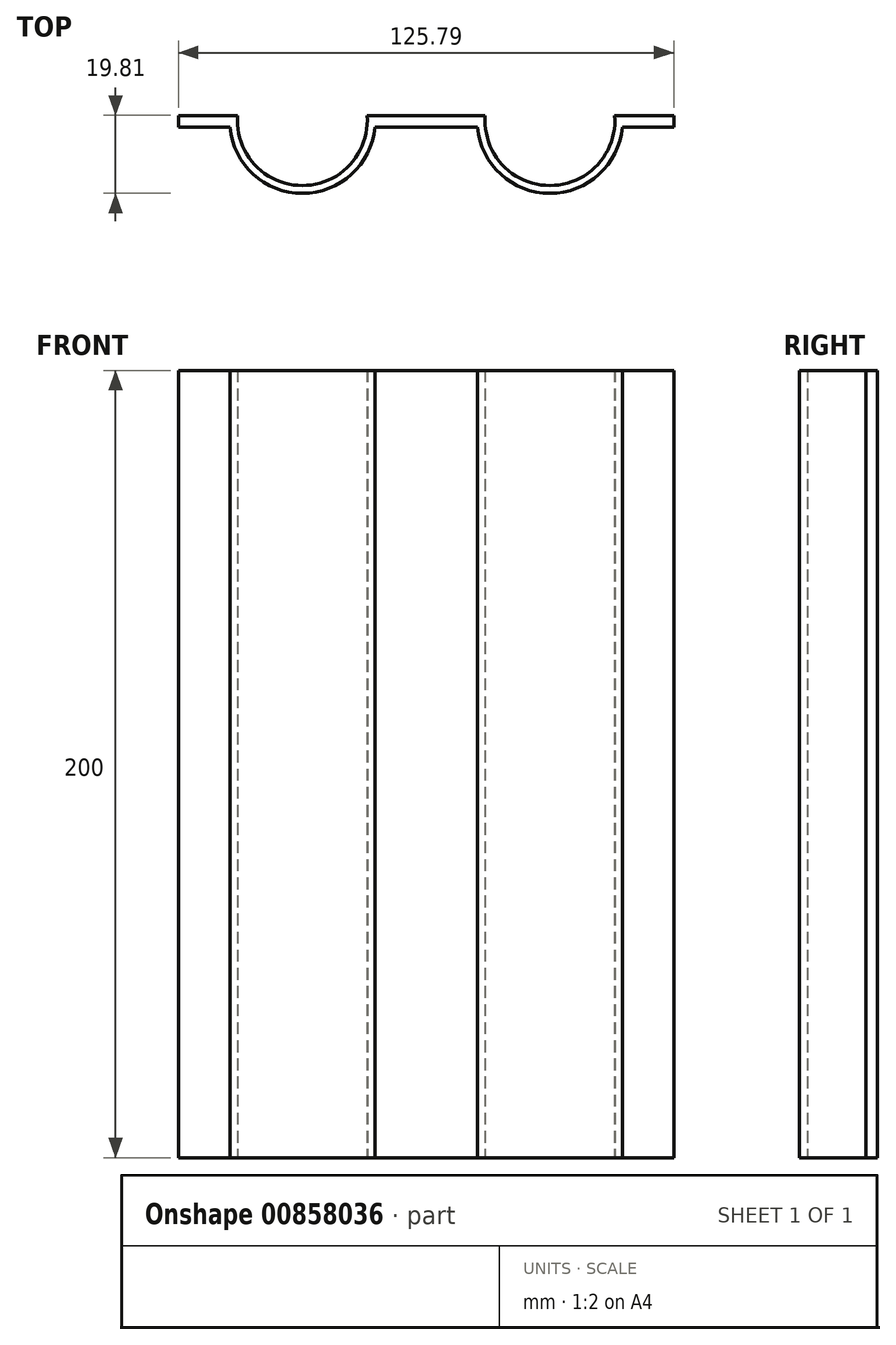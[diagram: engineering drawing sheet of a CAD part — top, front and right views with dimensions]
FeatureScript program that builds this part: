
annotation { "Feature Type Name" : "Feature", "Feature Type Description" : "" }
export const myFeature = defineFeature(function(context is Context, id is Id, definition is map)
    precondition{}
    {
        {
            var Q0;
            Q0=qCreatedBy(makeId("Top.planeOp"),FACE);
            var sketch = newSketch(context, id + "F0", { "sketchPlane" : qUnion([Q0])});
            skLineSegment(sketch, "E0", {"start": v(-51.2, 1.3) * mm, "end": v(-66.2, 1.3) * mm});
            skLineSegment(sketch, "E1", {"start": v(-66.2, 1.3) * mm, "end": v(-66.2, -1.7) * mm});
            skLineSegment(sketch, "E2", {"start": v(-66.2, -1.7) * mm, "end": v(-53.17, -1.7) * mm});
            skLineSegment(sketch, "E3", {"start": v(-18.3, 1.3) * mm, "end": v(11.7, 1.3) * mm});
            skLineSegment(sketch, "E4", {"start": v(44.6, 1.3) * mm, "end": v(59.6, 1.3) * mm});
            skLineSegment(sketch, "E5", {"start": v(59.6, 1.3) * mm, "end": v(59.6, -1.7) * mm});
            skLineSegment(sketch, "E6", {"start": v(59.6, -1.7) * mm, "end": v(46.57, -1.7) * mm});
            skLineSegment(sketch, "E7", {"start": v(9.72, -1.7) * mm, "end": v(-16.33, -1.7) * mm});
            skArc(sketch, "E8", {"start": v(-51.2, 1.3) * mm, "mid": v(-34.75, -16.5) * mm, "end": v(-18.3, 1.3) * mm});
            skArc(sketch, "E9", {"start": v(11.7, 1.3) * mm, "mid": v(28.15, -16.5) * mm, "end": v(44.6, 1.3) * mm});
            skArc(sketch, "E10.0", {"start": v(9.7, 1.47) * mm, "mid": v(9.7, 1.39) * mm, "end": v(9.7, 1.3) * mm});
            skArc(sketch, "E11.0", {"start": v(-53.2, 1.47) * mm, "mid": v(-53.2, 1.39) * mm, "end": v(-53.2, 1.3) * mm});
            skArc(sketch, "E12.trimOffspring", {"start": v(-53.17, -1.7) * mm, "mid": v(-34.75, -18.5) * mm, "end": v(-16.33, -1.7) * mm});
            skPoint(sketch, "E13.orphan", {"position": v(-51.16, -1.7) * mm});
            skArc(sketch, "E14.trimOffspring", {"start": v(-16.3, 1.3) * mm, "mid": v(-16.3, 1.39) * mm, "end": v(-16.3, 1.47) * mm});
            skArc(sketch, "E15.trimOffspring", {"start": v(9.72, -1.7) * mm, "mid": v(28.15, -18.5) * mm, "end": v(46.57, -1.7) * mm});
            skArc(sketch, "E16.trimOffspring", {"start": v(46.6, 1.3) * mm, "mid": v(46.6, 1.39) * mm, "end": v(46.59, 1.47) * mm});
            skSolve(sketch);
        }
        {
            var Q0;
            {var subQ10=sQuery(id+"F0.wireOp",EDGE,"E1");Q0=makeQuery(id+"F0.imprint","IMPRINT",FACE,{"disambiguationData":[TD([[makeQuery(id+"F0.imprint","IMPRINT",EDGE,{"derivedFrom":subQ10}),1.0]])]});}
            extrude(context, id + "F1", {"entities" : qUnion([Q0]), "depth" : 100 * mm, "offsetDistance" : 25 * mm, "hasSecondDirection" : true, "secondDirectionOppositeDirection" : true, "secondDirectionDepth" : 100 * mm});
        }
    });
